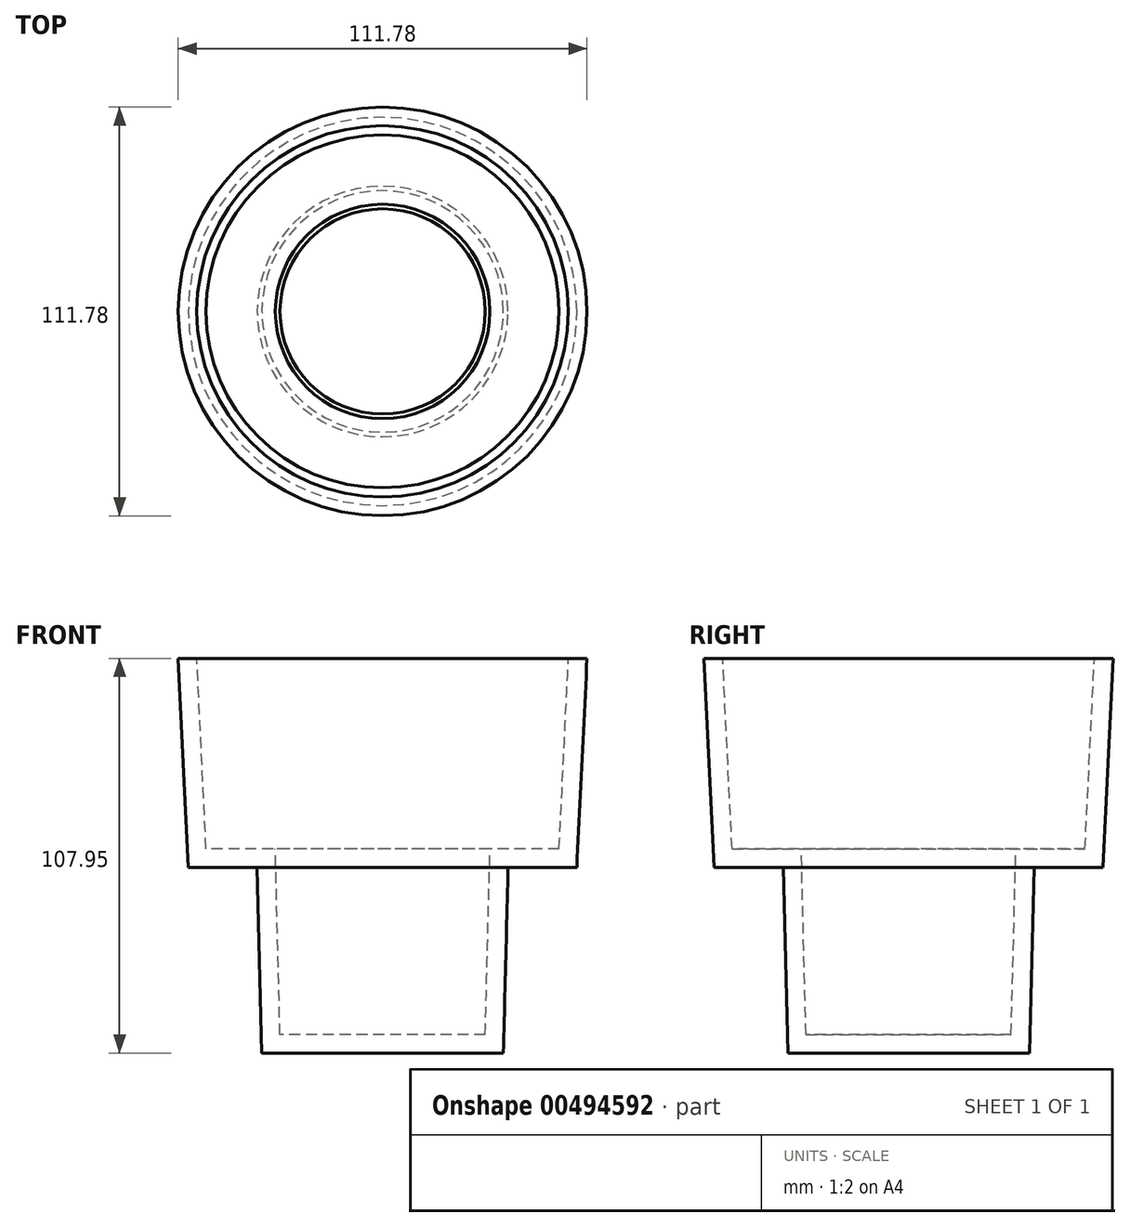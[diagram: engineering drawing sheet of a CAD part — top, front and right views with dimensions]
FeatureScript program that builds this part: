
annotation { "Feature Type Name" : "Feature", "Feature Type Description" : "" }
export const myFeature = defineFeature(function(context is Context, id is Id, definition is map)
    precondition{}
    {
        {
            var Q0;
            Q0=qCreatedBy(makeId("Front.planeOp"),FACE);
            var sketch = newSketch(context, id + "F0", { "sketchPlane" : qUnion([Q0])});
            skLineSegment(sketch, "E0", {"start": v(-34.3, 0) * mm, "end": v(-33.02, -50.8) * mm});
            skLineSegment(sketch, "E1", {"start": v(0, -50.8) * mm, "end": v(-33.02, -50.8) * mm});
            skLineSegment(sketch, "E2", {"start": v(-34.3, 0) * mm, "end": v(-53.1, 0) * mm});
            skLineSegment(sketch, "E3", {"start": v(-53.1, 0) * mm, "end": v(-55.89, 57.15) * mm});
            skLineSegment(sketch, "E4", {"start": v(0, 57.15) * mm, "end": v(0, -50.8) * mm});
            skLineSegment(sketch, "E5.0", {"start": v(-48.26, 5.08) * mm, "end": v(-50.8, 57.15) * mm});
            skLineSegment(sketch, "E5.1", {"start": v(-29.34, 5.08) * mm, "end": v(-48.26, 5.08) * mm});
            skLineSegment(sketch, "E5.2", {"start": v(-29.34, 5.08) * mm, "end": v(-28.07, -45.72) * mm});
            skLineSegment(sketch, "E5.3", {"start": v(0, -45.72) * mm, "end": v(-28.07, -45.72) * mm});
            skLineSegment(sketch, "E6", {"start": v(-55.89, 57.15) * mm, "end": v(-50.8, 57.15) * mm});
            skLineSegment(sketch, "E7", {"start": v(-50.8, 57.15) * mm, "end": v(0, 57.15) * mm, "construction": true});
            skSolve(sketch);
        }
        {
            var Q0;
            Q0=makeQuery(id+"F0.imprint","IMPRINT",FACE,{"disambiguationData":[TD([[makeQuery(id+"F0.imprint","IMPRINT",EDGE,{"derivedFrom":sQuery(id+"F0.wireOp",EDGE,"E0")}),1.0]])]});
            var Q1;
            Q1=sQuery(id+"F0.wireOp",EDGE,"E4");
            revolve(context, id + "F1", {"entities" : qUnion([Q0]), "axis" : qUnion([Q1]), "revolveType" : RevolveType.FULL});
        }
    });
